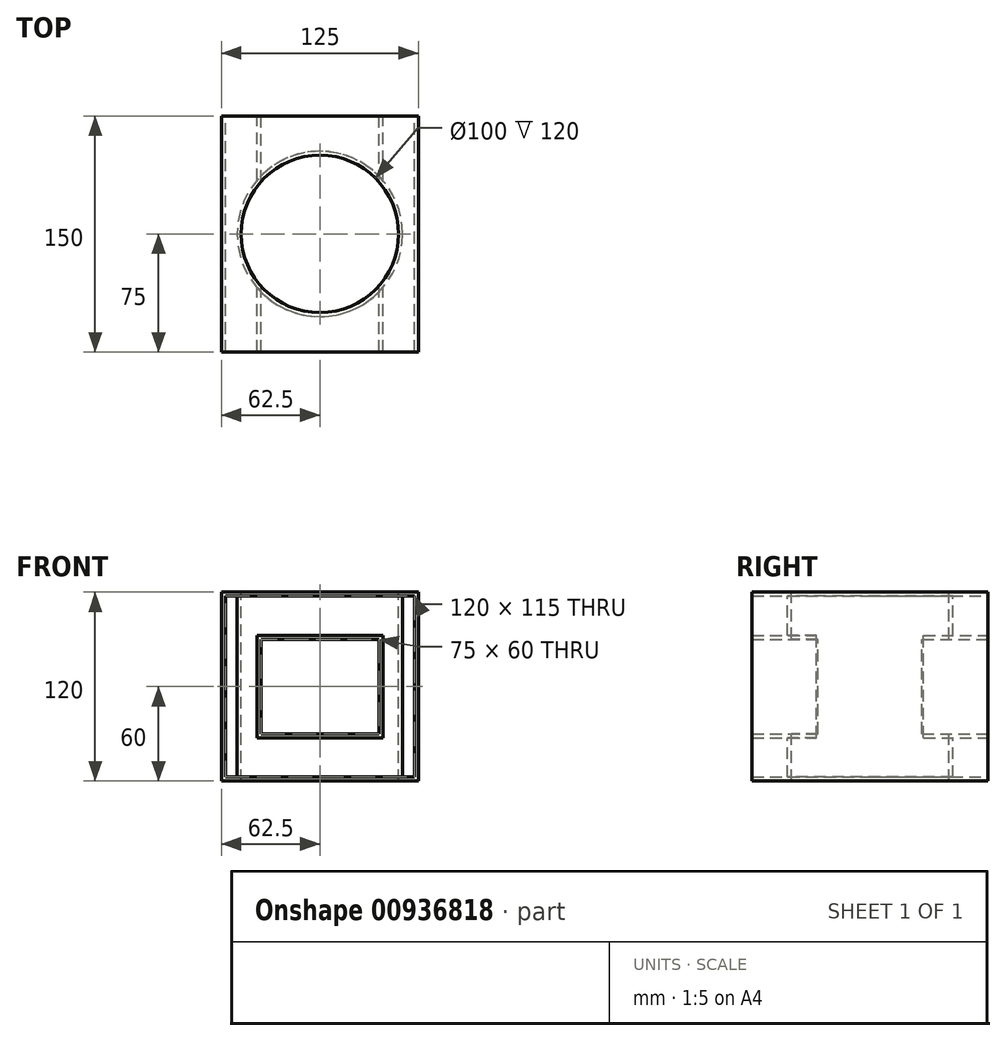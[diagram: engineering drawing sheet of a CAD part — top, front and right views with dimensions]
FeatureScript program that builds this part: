
annotation { "Feature Type Name" : "Feature", "Feature Type Description" : "" }
export const myFeature = defineFeature(function(context is Context, id is Id, definition is map)
    precondition{}
    {
        {
            var Q0;
            Q0=qCreatedBy(makeId("Front.planeOp"),FACE);
            var sketch = newSketch(context, id + "F0", { "sketchPlane" : qUnion([Q0])});
            skLineSegment(sketch, "E0.bottom", {"start": v(0, 0) * mm, "end": v(125, 0) * mm});
            skLineSegment(sketch, "E0.top", {"start": v(0, 120) * mm, "end": v(125, 120) * mm});
            skLineSegment(sketch, "E0.left", {"start": v(0, 0) * mm, "end": v(0, 120) * mm});
            skLineSegment(sketch, "E0.right", {"start": v(125, 0) * mm, "end": v(125, 120) * mm});
            skLineSegment(sketch, "E1.bottom", {"start": v(100, 30) * mm, "end": v(25, 30) * mm});
            skLineSegment(sketch, "E1.top", {"start": v(100, 90) * mm, "end": v(25, 90) * mm});
            skLineSegment(sketch, "E1.left", {"start": v(100, 30) * mm, "end": v(100, 90) * mm});
            skLineSegment(sketch, "E1.right", {"start": v(25, 30) * mm, "end": v(25, 90) * mm});
            skSolve(sketch);
        }
        {
            var Q0;
            Q0 = qSketchRegion(id + "F0", true);
            extrude(context, id + "F1", {"entities" : qUnion([Q0]), "depth" : 150 * mm, "offsetDistance" : 25 * mm});
        }
        {
            var Q0;
            Q0=makeQuery(id+"F1.opExtrude","SWEPT_FACE",FACE,{"disambiguationData":[OSD([sQuery(id+"F0.wireOp",EDGE,"E0.top")])]});
            var sketch = newSketch(context, id + "F2", { "sketchPlane" : qUnion([Q0])});
            skLineSegment(sketch, "E2", {"start": v(125, -150) * mm, "end": v(0, 0) * mm, "construction": true});
            skPoint(sketch, "E3", {"position": v(62.5, -75) * mm});
            skCircle(sketch, "E4", {"center": v(62.5, -75) * mm, "radius": 50 * mm});
            skSolve(sketch);
        }
        {
            var Q0;
            Q0 = qSketchRegion(id + "F2", true);
            extrude(context, id + "F3", {"entities" : qUnion([Q0]), "operationType" : NewBodyOperationType.REMOVE, "endBound" : BoundingType.THROUGH_ALL, "oppositeDirection" : true, "depth" : 25 * mm, "offsetDistance" : 25 * mm});
        }
        {
            var Q0;
            Q0=makeQuery(id+"F1.opExtrude","CAP_FACE",FACE,{"disambiguationData":[OSD([sQuery(id+"F0.wireOp",EDGE,"E0.bottom"),sQuery(id+"F0.wireOp",EDGE,"E0.top"),sQuery(id+"F0.wireOp",EDGE,"E0.left"),sQuery(id+"F0.wireOp",EDGE,"E0.right"),sQuery(id+"F0.wireOp",EDGE,"E1.bottom"),sQuery(id+"F0.wireOp",EDGE,"E1.top"),sQuery(id+"F0.wireOp",EDGE,"E1.left"),sQuery(id+"F0.wireOp",EDGE,"E1.right")])],"isStart":false});
            var Q1;
            Q1=makeQuery(id+"F1.opExtrude","CAP_FACE",FACE,{"disambiguationData":[OSD([sQuery(id+"F0.wireOp",EDGE,"E0.bottom"),sQuery(id+"F0.wireOp",EDGE,"E0.top"),sQuery(id+"F0.wireOp",EDGE,"E0.left"),sQuery(id+"F0.wireOp",EDGE,"E0.right"),sQuery(id+"F0.wireOp",EDGE,"E1.bottom"),sQuery(id+"F0.wireOp",EDGE,"E1.top"),sQuery(id+"F0.wireOp",EDGE,"E1.left"),sQuery(id+"F0.wireOp",EDGE,"E1.right")])],"isStart":true});
            shell(context, id + "F4", {"entities" : qUnion([Q0, Q1]), "thickness" : 2.5 * mm});
        }
    });
